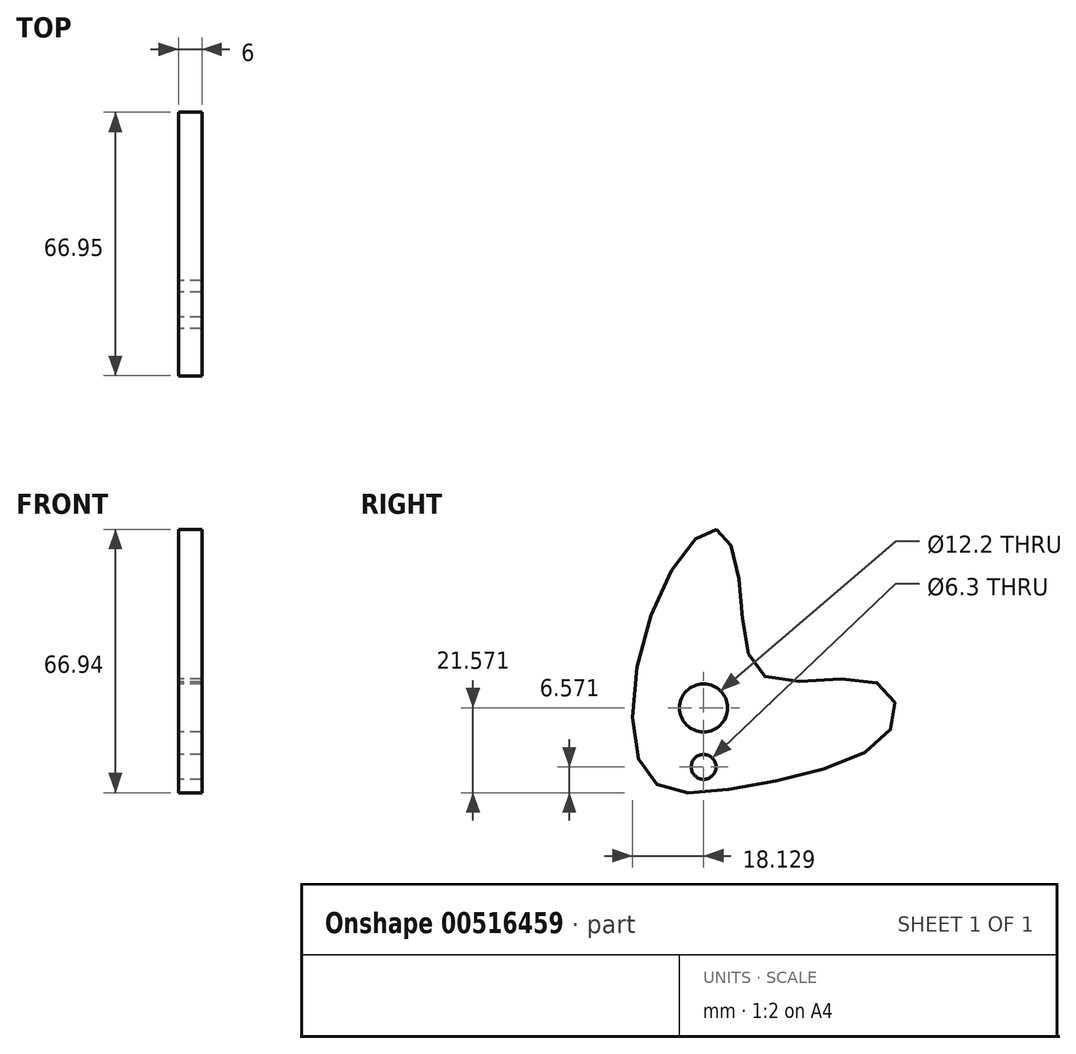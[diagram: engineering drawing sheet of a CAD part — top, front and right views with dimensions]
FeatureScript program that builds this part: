
annotation { "Feature Type Name" : "Feature", "Feature Type Description" : "" }
export const myFeature = defineFeature(function(context is Context, id is Id, definition is map)
    precondition{}
    {
        {
            var Q0;
            Q0=qCreatedBy(makeId("Right.planeOp"),FACE);
            var sketch = newSketch(context, id + "F0", { "sketchPlane" : qUnion([Q0])});
            skLineSegment(sketch, "E0", {"start": v(18.58, 1.68) * mm, "end": v(93.58, 1.68) * mm, "construction": true});
            skFitSpline(sketch, "E1", {"points": [v(21.8, 47) * mm, v(5.7, 26.62) * mm, v(4.28, -15.55) * mm, v(30.1, -18.15) * mm, v(65.87, -4.17) * mm, v(63.03, 7.9) * mm, v(34.36, 9.57) * mm, v(27.97, 30.89) * mm, v(21.8, 47) * mm]});
            skPoint(sketch, "E2.0", {"position": v(0, 0) * mm});
            skLineSegment(sketch, "E3", {"start": v(18.58, 1.68) * mm, "end": v(18.58, -13.32) * mm});
            skCircle(sketch, "E4", {"center": v(18.58, 1.68) * mm, "radius": 6.1 * mm});
            skSolve(sketch);
        }
        {
            var Q0;
            Q0=qCreatedBy(makeId("Right.planeOp"),FACE);
            var sketch = newSketch(context, id + "F1", { "sketchPlane" : qUnion([Q0])});
            skCircle(sketch, "E5", {"center": v(18.58, -13.32) * mm, "radius": 2 * mm});
            skSolve(sketch);
        }
        {
            var Q0;
            Q0=qCreatedBy(makeId("Right.planeOp"),FACE);
            var sketch = newSketch(context, id + "F2", { "sketchPlane" : qUnion([Q0])});
            skSolve(sketch);
        }
        {
            var Q0;
            Q0 = qSketchRegion(id + "F2", true);
            var Q1;
            Q1=makeQuery(id+"F0.imprint","IMPRINT",FACE,{"disambiguationData":[TD([[makeQuery(id+"F0.imprint","IMPRINT",EDGE,{"derivedFrom":sQuery(id+"F0.wireOp",EDGE,"E1")}),1.0]])]});
            extrude(context, id + "F3", {"entities" : qUnion([Q0, Q1]), "depth" : 6 * mm, "offsetDistance" : 25 * mm});
        }
        {
            var Q0;
            Q0=makeQuery(id+"F1.imprint","IMPRINT",FACE,{"disambiguationData":[TD([[makeQuery(id+"F1.imprint","IMPRINT",EDGE,{"derivedFrom":sQuery(id+"F1.wireOp",EDGE,"E5")}),1.0]])]});
            extrude(context, id + "F4", {"entities" : qUnion([Q0]), "operationType" : NewBodyOperationType.REMOVE, "depth" : 6 * mm, "offsetDistance" : 25 * mm});
        }
        {
            var Q0;
            Q0=qCreatedBy(makeId("Right.planeOp"),FACE);
            var sketch = newSketch(context, id + "F5", { "sketchPlane" : qUnion([Q0])});
            skCircle(sketch, "E6", {"center": v(18.58, -13.32) * mm, "radius": 3.15 * mm});
            skSolve(sketch);
        }
        {
            var Q0;
            Q0=makeQuery(id+"F5.imprint","IMPRINT",FACE,{"disambiguationData":[TD([[makeQuery(id+"F5.imprint","IMPRINT",EDGE,{"derivedFrom":sQuery(id+"F5.wireOp",EDGE,"E6")}),1.0]])]});
            extrude(context, id + "F6", {"entities" : qUnion([Q0]), "operationType" : NewBodyOperationType.REMOVE, "depth" : 6 * mm, "offsetDistance" : 25 * mm});
        }
    });
